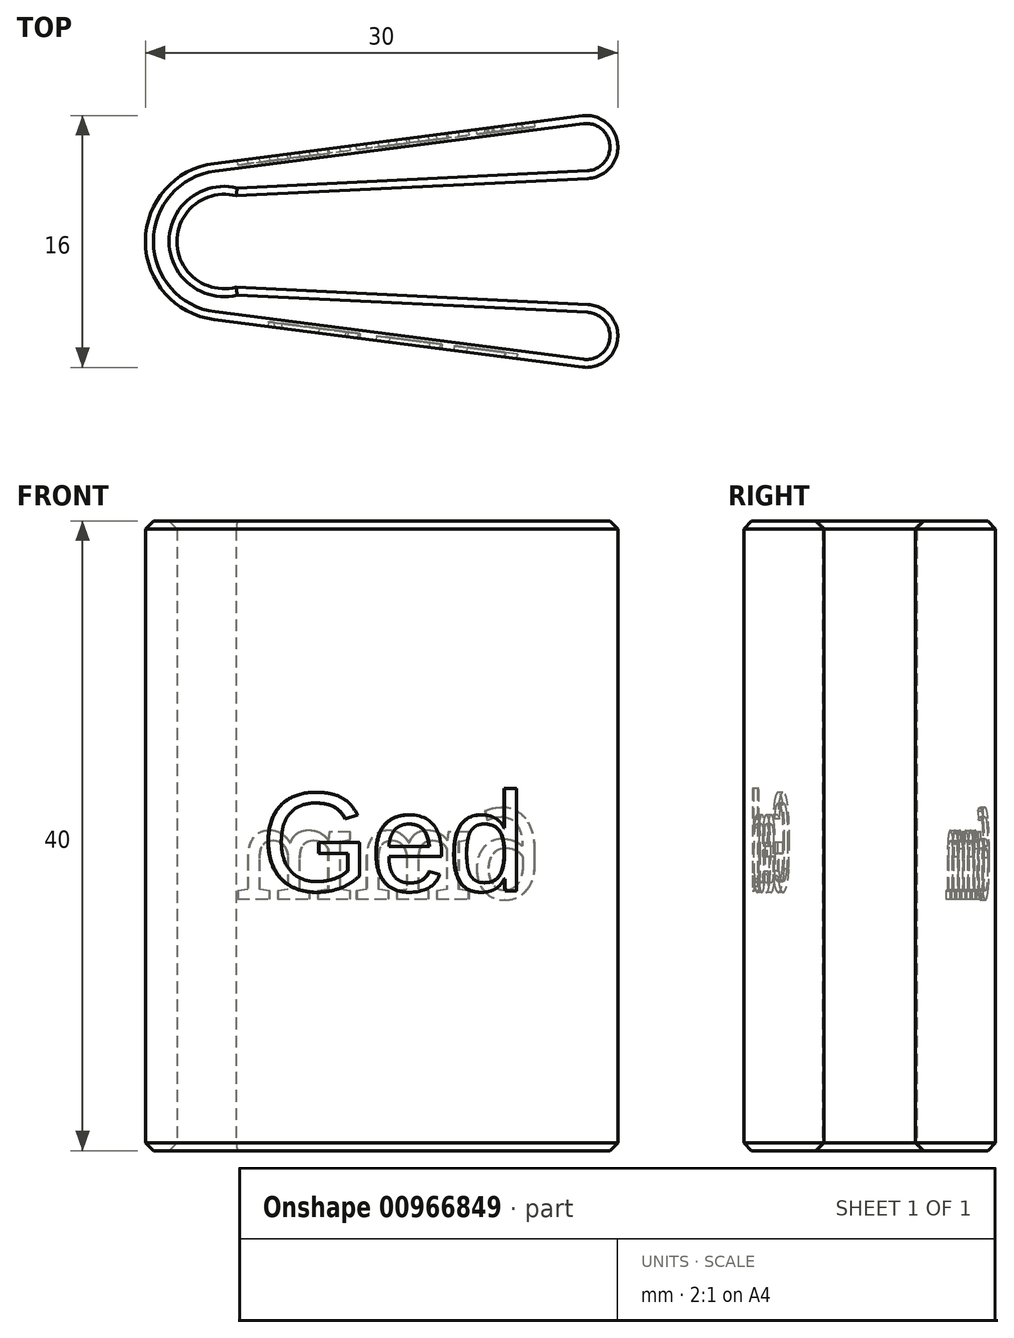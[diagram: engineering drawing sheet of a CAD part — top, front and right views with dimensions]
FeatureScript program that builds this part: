
annotation { "Feature Type Name" : "Feature", "Feature Type Description" : "" }
export const myFeature = defineFeature(function(context is Context, id is Id, definition is map)
    precondition{}
    {
        {
            var Q0;
            Q0=qCreatedBy(makeId("Top.planeOp"),FACE);
            var sketch = newSketch(context, id + "F0", { "sketchPlane" : qUnion([Q0])});
            skArc(sketch, "E0", {"start": v(0.77, 2.9) * mm, "mid": v(-3, 0) * mm, "end": v(0.77, -2.9) * mm});
            skArc(sketch, "E1", {"start": v(-0.64, 4.96) * mm, "mid": v(-5, 0) * mm, "end": v(-0.64, -4.96) * mm});
            skLineSegment(sketch, "E2", {"start": v(0.77, 2.9) * mm, "end": v(23.1, 4) * mm});
            skLineSegment(sketch, "E3", {"start": v(0.77, -2.9) * mm, "end": v(23.1, -4) * mm});
            skLineSegment(sketch, "E4", {"start": v(-0.64, 4.96) * mm, "end": v(22.74, 7.98) * mm});
            skLineSegment(sketch, "E5", {"start": v(-0.64, -4.96) * mm, "end": v(22.74, -7.98) * mm});
            skLineSegment(sketch, "E6", {"start": v(25, 6) * mm, "end": v(25, 6) * mm});
            skArc(sketch, "E7.filletArc", {"start": v(25, 6) * mm, "mid": v(24.32, 7.5) * mm, "end": v(22.74, 7.98) * mm});
            skLineSegment(sketch, "E8.trimOffspring", {"start": v(25, -6) * mm, "end": v(25, -6) * mm});
            skArc(sketch, "E9.filletArc", {"start": v(23.1, 4) * mm, "mid": v(24.45, 4.62) * mm, "end": v(25, 6) * mm});
            skArc(sketch, "E10.filletArc", {"start": v(25, -6) * mm, "mid": v(24.45, -4.62) * mm, "end": v(23.1, -4) * mm});
            skArc(sketch, "E11.filletArc", {"start": v(22.74, -7.98) * mm, "mid": v(24.32, -7.5) * mm, "end": v(25, -6) * mm});
            skSolve(sketch);
        }
        {
            var Q0;
            Q0=makeQuery(id+"F0.imprint","IMPRINT",FACE,{"disambiguationData":[TD([[makeQuery(id+"F0.imprint","IMPRINT",EDGE,{"derivedFrom":sQuery(id+"F0.wireOp",EDGE,"E0")}),-1.0]])]});
            extrude(context, id + "F1", {"entities" : qUnion([Q0]), "depth" : 40 * mm, "offsetDistance" : 25 * mm});
        }
        {
            var Q0;
            Q0=makeQuery(id+"F1.opExtrude","CAP_FACE",FACE,{"disambiguationData":[OSD([sQuery(id+"F0.wireOp",EDGE,"E0"),sQuery(id+"F0.wireOp",EDGE,"E1"),sQuery(id+"F0.wireOp",EDGE,"E2"),sQuery(id+"F0.wireOp",EDGE,"E3"),sQuery(id+"F0.wireOp",EDGE,"E4"),sQuery(id+"F0.wireOp",EDGE,"E5"),sQuery(id+"F0.wireOp",EDGE,"E7.filletArc"),sQuery(id+"F0.wireOp",EDGE,"E9.filletArc"),sQuery(id+"F0.wireOp",EDGE,"E10.filletArc"),sQuery(id+"F0.wireOp",EDGE,"E11.filletArc")])],"isStart":false});
            var Q1;
            Q1=makeQuery(id+"F1.opExtrude","CAP_FACE",FACE,{"disambiguationData":[OSD([sQuery(id+"F0.wireOp",EDGE,"E0"),sQuery(id+"F0.wireOp",EDGE,"E1"),sQuery(id+"F0.wireOp",EDGE,"E2"),sQuery(id+"F0.wireOp",EDGE,"E3"),sQuery(id+"F0.wireOp",EDGE,"E4"),sQuery(id+"F0.wireOp",EDGE,"E5"),sQuery(id+"F0.wireOp",EDGE,"E7.filletArc"),sQuery(id+"F0.wireOp",EDGE,"E9.filletArc"),sQuery(id+"F0.wireOp",EDGE,"E10.filletArc"),sQuery(id+"F0.wireOp",EDGE,"E11.filletArc")])],"isStart":true});
            chamfer(context, id + "F2", {"entities" : qUnion([Q0, Q1]), "width" : 0.5 * mm, "tangentPropagation" : true});
        }
        {
            var Q0;
            Q0=makeQuery(id+"F1.opExtrude","SWEPT_FACE",FACE,{"disambiguationData":[OSD([sQuery(id+"F0.wireOp",EDGE,"E5")])]});
            var sketch = newSketch(context, id + "F3", { "sketchPlane" : qUnion([Q0])});
            skText(sketch, "E12", { "text": "Ged", "fontName": "Arimo-Regular.ttf"});
            const initialGuessF3  = {"E12": [0.003, 0.0165, 1, 0, 0.00646]};
            skSetInitialGuess(sketch, initialGuessF3);
            skSolve(sketch);
        }
        {
            var Q0;
            Q0=makeQuery(id+"F3.imprint","IMPRINT",FACE,{"disambiguationData":[TD([[makeQuery(id+"F3.imprint","IMPRINT",EDGE,{"derivedFrom":sQuery(id+"F3.wireOp",EDGE,"E12.sketch_text.stroke-0")}),-1.0]])]});
            var Q1;
            Q1=makeQuery(id+"F3.imprint","IMPRINT",FACE,{"disambiguationData":[TD([[makeQuery(id+"F3.imprint","IMPRINT",EDGE,{"derivedFrom":sQuery(id+"F3.wireOp",EDGE,"E12.sketch_text.stroke-23")}),-1.0]])]});
            var Q2;
            Q2=makeQuery(id+"F3.imprint","IMPRINT",FACE,{"disambiguationData":[TD([[makeQuery(id+"F3.imprint","IMPRINT",EDGE,{"derivedFrom":sQuery(id+"F3.wireOp",EDGE,"E12.sketch_text.stroke-41")}),-1.0]])]});
            extrude(context, id + "F4", {"entities" : qUnion([Q0, Q1, Q2]), "operationType" : NewBodyOperationType.REMOVE, "oppositeDirection" : true, "depth" : 0.3 * mm, "offsetDistance" : 25 * mm});
        }
        {
            var Q0;
            Q0=makeQuery(id+"F1.opExtrude","SWEPT_FACE",FACE,{"disambiguationData":[OSD([sQuery(id+"F0.wireOp",EDGE,"E4")])]});
            var sketch = newSketch(context, id + "F5", { "sketchPlane" : qUnion([Q0])});
            skText(sketch, "E13", { "text": "6mm", "fontName": "RobotoSlab-Regular.ttf"});
            const initialGuessF5  = {"E13": [-0.021, 0.016, 1, 0, 0.0058]};
            skSetInitialGuess(sketch, initialGuessF5);
            skSolve(sketch);
        }
        {
            var Q0;
            Q0=makeQuery(id+"F5.imprint","IMPRINT",FACE,{"disambiguationData":[TD([[makeQuery(id+"F5.imprint","IMPRINT",EDGE,{"derivedFrom":sQuery(id+"F5.wireOp",EDGE,"E13.sketch_text.stroke-69")}),-1.0]])]});
            var Q1;
            Q1=makeQuery(id+"F5.imprint","IMPRINT",FACE,{"disambiguationData":[TD([[makeQuery(id+"F5.imprint","IMPRINT",EDGE,{"derivedFrom":sQuery(id+"F5.wireOp",EDGE,"E13.sketch_text.stroke-28")}),-1.0]])]});
            var Q2;
            Q2=makeQuery(id+"F5.imprint","IMPRINT",FACE,{"disambiguationData":[TD([[makeQuery(id+"F5.imprint","IMPRINT",EDGE,{"derivedFrom":sQuery(id+"F5.wireOp",EDGE,"E13.sketch_text.stroke-0")}),-1.0]])]});
            extrude(context, id + "F6", {"entities" : qUnion([Q0, Q1, Q2]), "operationType" : NewBodyOperationType.REMOVE, "oppositeDirection" : true, "depth" : 0.3 * mm, "offsetDistance" : 25 * mm});
        }
    });
